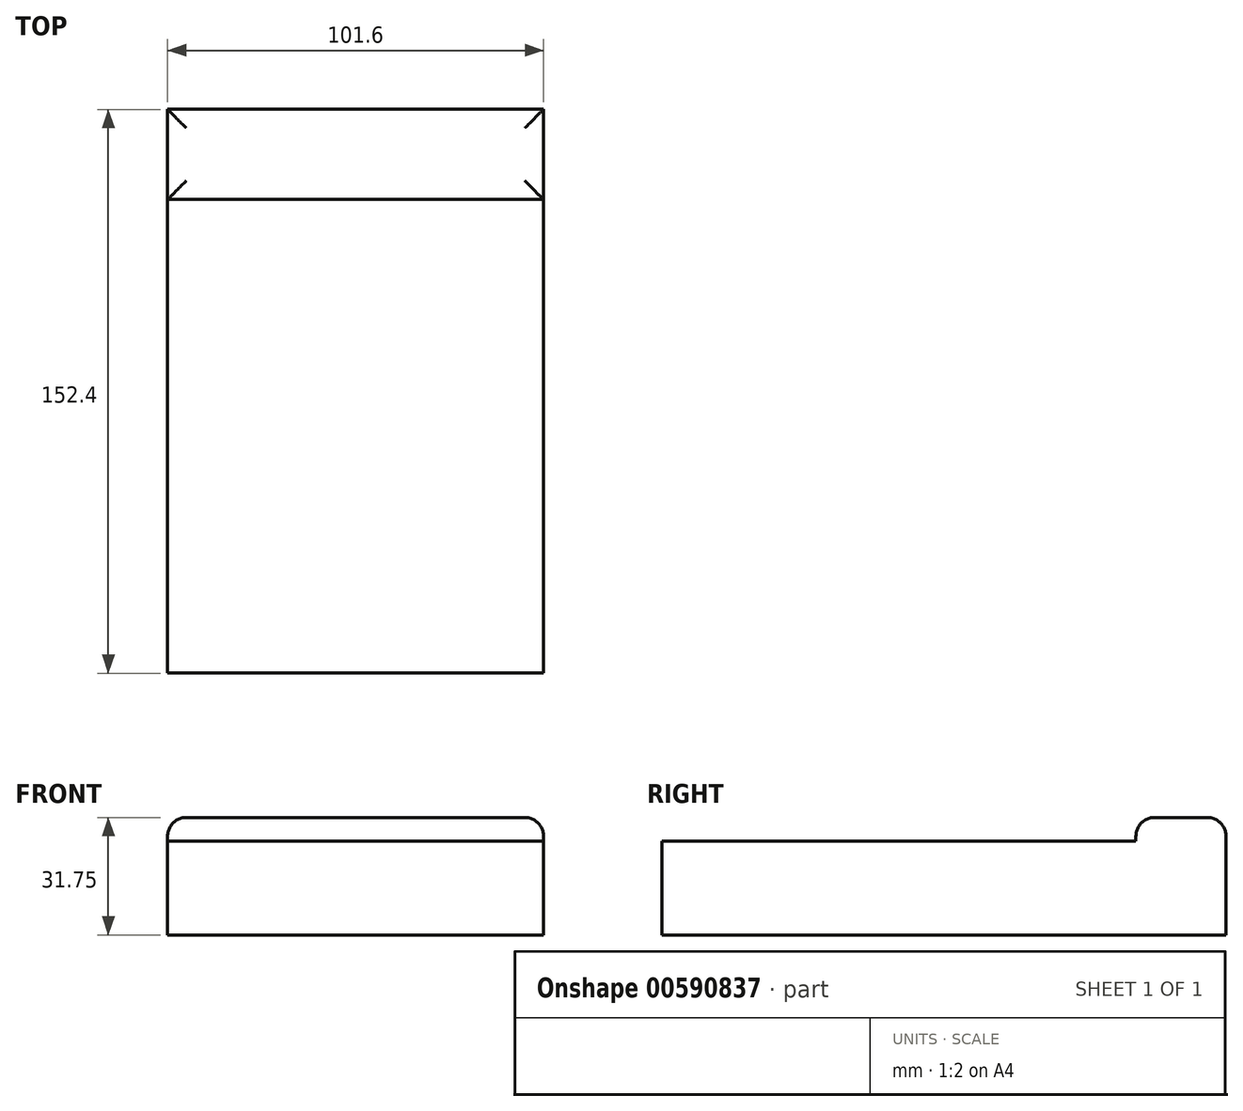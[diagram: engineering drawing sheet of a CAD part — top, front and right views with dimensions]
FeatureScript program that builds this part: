
annotation { "Feature Type Name" : "Feature", "Feature Type Description" : "" }
export const myFeature = defineFeature(function(context is Context, id is Id, definition is map)
    precondition{}
    {
        {
            var Q0;
            Q0=qCreatedBy(makeId("Top.planeOp"),FACE);
            var sketch = newSketch(context, id + "F0", { "sketchPlane" : qUnion([Q0])});
            skLineSegment(sketch, "E0", {"start": v(-49.8, 107.26) * mm, "end": v(51.8, 107.26) * mm});
            skLineSegment(sketch, "E1", {"start": v(51.8, 107.26) * mm, "end": v(51.8, -45.14) * mm});
            skLineSegment(sketch, "E2", {"start": v(51.8, -45.14) * mm, "end": v(-49.8, -45.14) * mm});
            skLineSegment(sketch, "E3", {"start": v(-49.8, -45.14) * mm, "end": v(-49.8, 107.26) * mm});
            skSolve(sketch);
        }
        {
            var Q0;
            Q0=makeQuery(id+"F0.imprint","IMPRINT",FACE,{"disambiguationData":[TD([[makeQuery(id+"F0.imprint","IMPRINT",EDGE,{"derivedFrom":sQuery(id+"F0.wireOp",EDGE,"E0")}),-1.0]])]});
            extrude(context, id + "F1", {"entities" : qUnion([Q0]), "depth" : 25.4 * mm, "offsetDistance" : 25.4 * mm});
        }
        {
            var Q0;
            Q0=makeQuery(id+"F1.opExtrude","CAP_FACE",FACE,{"disambiguationData":[OSD([sQuery(id+"F0.wireOp",EDGE,"E0"),sQuery(id+"F0.wireOp",EDGE,"E1"),sQuery(id+"F0.wireOp",EDGE,"E2"),sQuery(id+"F0.wireOp",EDGE,"E3")])],"isStart":false});
            var sketch = newSketch(context, id + "F2", { "sketchPlane" : qUnion([Q0])});
            skLineSegment(sketch, "E4", {"start": v(-49.8, 82.9) * mm, "end": v(0, 82.9) * mm});
            skLineSegment(sketch, "E5", {"start": v(0, 82.9) * mm, "end": v(0, 107.26) * mm});
            skLineSegment(sketch, "E6", {"start": v(0, 107.26) * mm, "end": v(51.8, 107.26) * mm});
            skLineSegment(sketch, "E7", {"start": v(51.8, 107.26) * mm, "end": v(51.8, 82.9) * mm});
            skLineSegment(sketch, "E8", {"start": v(51.8, 82.9) * mm, "end": v(-8.91, 82.9) * mm});
            skLineSegment(sketch, "E9", {"start": v(-8.91, 82.9) * mm, "end": v(-49.8, 82.9) * mm});
            skLineSegment(sketch, "E10", {"start": v(-49.8, 107.26) * mm, "end": v(0, 107.26) * mm});
            skSolve(sketch);
        }
        {
            var Q0;
            {var subQ2=sQuery(id+"F2.wireOp",EDGE,"E5");Q0=makeQuery(id+"F2.imprint","IMPRINT",FACE,{"disambiguationData":[TD([[makeQuery(id+"F2.imprint","IMPRINT",EDGE,{"derivedFrom":subQ2}),1.0]])]});}
            extrude(context, id + "F3", {"entities" : qUnion([Q0]), "operationType" : NewBodyOperationType.ADD, "depth" : 6.35 * mm, "offsetDistance" : 25.4 * mm});
        }
        {
            var Q0;
            {var subQ0=sQuery(id+"F2.wireOp",EDGE,"E5");Q0=makeQuery(id+"F2.imprint","IMPRINT",FACE,{"disambiguationData":[TD([[makeQuery(id+"F2.imprint","IMPRINT",EDGE,{"derivedFrom":subQ0}),-1.0]])]});}
            extrude(context, id + "F4", {"entities" : qUnion([Q0]), "operationType" : NewBodyOperationType.ADD, "depth" : 6.35 * mm, "offsetDistance" : 25.4 * mm});
        }
        {
            var Q0;
            Q0=makeQuery(id+"F3.opExtrude","CAP_EDGE",EDGE,{"disambiguationData":[OSD([sQuery(id+"F0.wireOp",EDGE,"E3")])],"isStart":false});
            var Q1;
            {var subQ0=sQuery(id+"F2.wireOp",EDGE,"E8");Q1=makeQuery(id+"F4.boolean.opBoolean","MERGE",EDGE,{"derivedFrom":[makeQuery(id+"F3.opExtrude","CAP_EDGE",EDGE,{"disambiguationData":[OSD([subQ0,sQuery(id+"F2.wireOp",EDGE,"E9")])],"isStart":false}),makeQuery(id+"F4.opExtrude","CAP_EDGE",EDGE,{"disambiguationData":[OSD([subQ0])],"isStart":false})]});}
            var Q2;
            {var subQ0=sQuery(id+"F2.wireOp",EDGE,"E8");var subQ1=sQuery(id+"F2.wireOp",EDGE,"E5");Q2=makeQuery(id+"F4.boolean.opBoolean","MERGE",FACE,{"derivedFrom":[makeQuery(id+"F3.opExtrude","CAP_FACE",FACE,{"disambiguationData":[OSD([sQuery(id+"F0.wireOp",EDGE,"E3"),subQ1,subQ0,sQuery(id+"F2.wireOp",EDGE,"E9"),sQuery(id+"F2.wireOp",EDGE,"E10")])],"isStart":false}),makeQuery(id+"F4.opExtrude","CAP_FACE",FACE,{"disambiguationData":[OSD([subQ1,sQuery(id+"F2.wireOp",EDGE,"E6"),sQuery(id+"F2.wireOp",EDGE,"E7"),subQ0])],"isStart":false})]});}
            fillet(context, id + "F5", {"entities" : qUnion([Q0, Q1, Q2]), "radius" : 5.08 * mm, "tangentPropagation" : true, "allowEdgeOverflow" : false});
        }
    });
